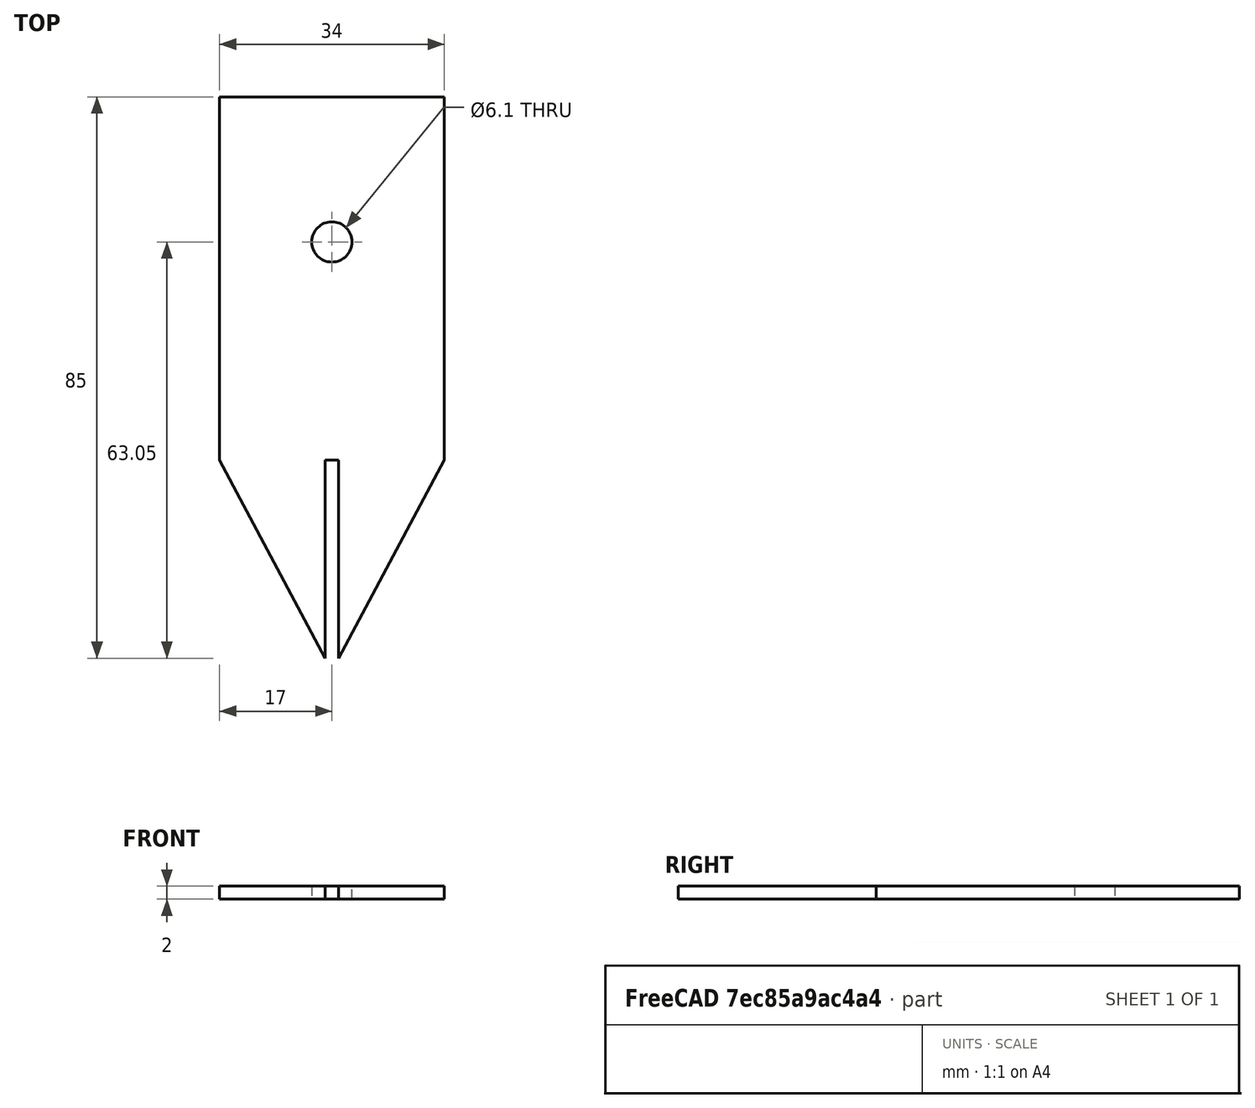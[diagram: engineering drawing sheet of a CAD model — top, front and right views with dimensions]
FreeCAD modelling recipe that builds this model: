
FCSTD DOCUMENT  (FreeCAD 0.19R24291 (Git))
Label: Gauge
License: All rights reserved
LicenseURL: http://en.wikipedia.org/wiki/All_rights_reserved
objects: Sketcher::SketchObject×1, PartDesign::Pad×1, PartDesign::Body×1
note: 4 computed .brp shape members not serialized (recipe doc carries the construction recipe); baked Part::Feature solids carry a one-line shape summary decoded from their .brp

FEATURE [Sketcher::SketchObject] Sketch
  FullyConstrained = true
  MapMode = 5
  Support = -> [XY_Plane]
  sketch-geometry (23):
    g0: GeomPoint X=-17 Y=0 Z=0
    g1: GeomPoint X=17 Y=0 Z=0
    g2: GeomPoint X=-1 Y=-30 Z=0
    g3: GeomPoint X=1 Y=-30 Z=0
    g4: GeomPoint X=-17 Y=55 Z=0
    g5: GeomPoint X=17 Y=55 Z=0
    g6: LineSegment StartX=-17 StartY=0 StartZ=0 EndX=-17 EndY=55 EndZ=0
    g7: LineSegment StartX=17 StartY=0 StartZ=0 EndX=17 EndY=55 EndZ=0
    g8: LineSegment StartX=-17 StartY=55 StartZ=0 EndX=17 EndY=55 EndZ=0
    g9: LineSegment StartX=-17 StartY=0 StartZ=0 EndX=-1 EndY=-30 EndZ=0
    g10: LineSegment StartX=17 StartY=0 StartZ=0 EndX=1 EndY=-30 EndZ=0
    g11: LineSegment StartX=-1 StartY=-30 StartZ=0 EndX=-1 EndY=0 EndZ=0
    g12: LineSegment StartX=1 StartY=-30 StartZ=0 EndX=1 EndY=0 EndZ=0
    g13: LineSegment StartX=1 StartY=0 StartZ=0 EndX=-1 EndY=0 EndZ=0
    g14: LineSegment StartX=-17 StartY=55 StartZ=0 EndX=-17 EndY=0 EndZ=0
    g15: LineSegment StartX=-17 StartY=0 StartZ=0 EndX=-1 EndY=-30 EndZ=0
    g16: LineSegment StartX=-1 StartY=-30 StartZ=0 EndX=-1 EndY=0 EndZ=0
    g17: LineSegment StartX=-1 StartY=0 StartZ=0 EndX=1 EndY=0 EndZ=0
    g18: LineSegment StartX=1 StartY=0 StartZ=0 EndX=1 EndY=-30 EndZ=0
    g19: LineSegment StartX=1 StartY=-30 StartZ=0 EndX=17 EndY=0 EndZ=0
    g20: LineSegment StartX=17 StartY=0 StartZ=0 EndX=17 EndY=55 EndZ=0
    g21: LineSegment StartX=17 StartY=55 StartZ=0 EndX=-17 EndY=55 EndZ=0
    g22: Circle CenterX=0 CenterY=33.05 CenterZ=0 NormalX=0 NormalY=0 NormalZ=1 AngleXU=0 Radius=3.05
  constraints (49):
    c: PointOnObject(g0,g-1)
    c: PointOnObject(g1,g-1)
    c: Distance(g-1,g0) = 17
    c: Distance(g1,g-1) = 17
    c: Distance(g4,g-2) = 17
    c: Distance(g5,g-2) = 17
    c: Distance(g2,g-2) = 1
    c: Distance(g3,g-2) = 1
    c: Coincident(g6,g0)
    c: Coincident(g6,g4)
    c: Coincident(g7,g1)
    c: Coincident(g7,g5)
    c: DistanceY(g6,g6) = 55
    c: DistanceY(g7,g7) = 55
    c: Coincident(g8,g4)
    c: Coincident(g8,g5)
    c: DistanceY(g2,g-1) = 30
    c: DistanceY(g3,g-1) = 30
    c: Coincident(g9,g0)
    c: Coincident(g9,g2)
    c: Coincident(g10,g1)
    c: Coincident(g10,g3)
    c: Coincident(g11,g2)
    c: PointOnObject(g11,g-1)
    c: Vertical(g11)
    c: Coincident(g12,g3)
    c: PointOnObject(g12,g-1)
    c: Vertical(g12)
    c: Coincident(g13,g12)
    c: Coincident(g13,g11)
    c: Coincident(g14,g4)
    c: Coincident(g14,g0)
    c: Coincident(g14,g15)
    c: Coincident(g15,g2)
    c: Coincident(g15,g16)
    c: Coincident(g16,g11)
    c: Coincident(g16,g17)
    c: Coincident(g17,g12)
    c: Coincident(g17,g18)
    c: Coincident(g18,g3)
    c: Coincident(g18,g19)
    c: Coincident(g19,g1)
    c: Coincident(g19,g20)
    c: Coincident(g20,g5)
    c: Coincident(g20,g21)
    c: Coincident(g21,g14)
    c: PointOnObject(g22,g-2)
    c: Diameter(g22) = 6.1
    c: Distance(g22,g-1) = 33.05
FEATURE [PartDesign::Pad] Pad
  Direction = (1,1,1)
  Length = 2
  Length2 = 100
  Profile = -> Sketch
  Type = 0
FEATURE [PartDesign::Body] Body
  Group = -> [Sketch,Pad]
  Origin = -> Origin
  Tip = -> Pad
